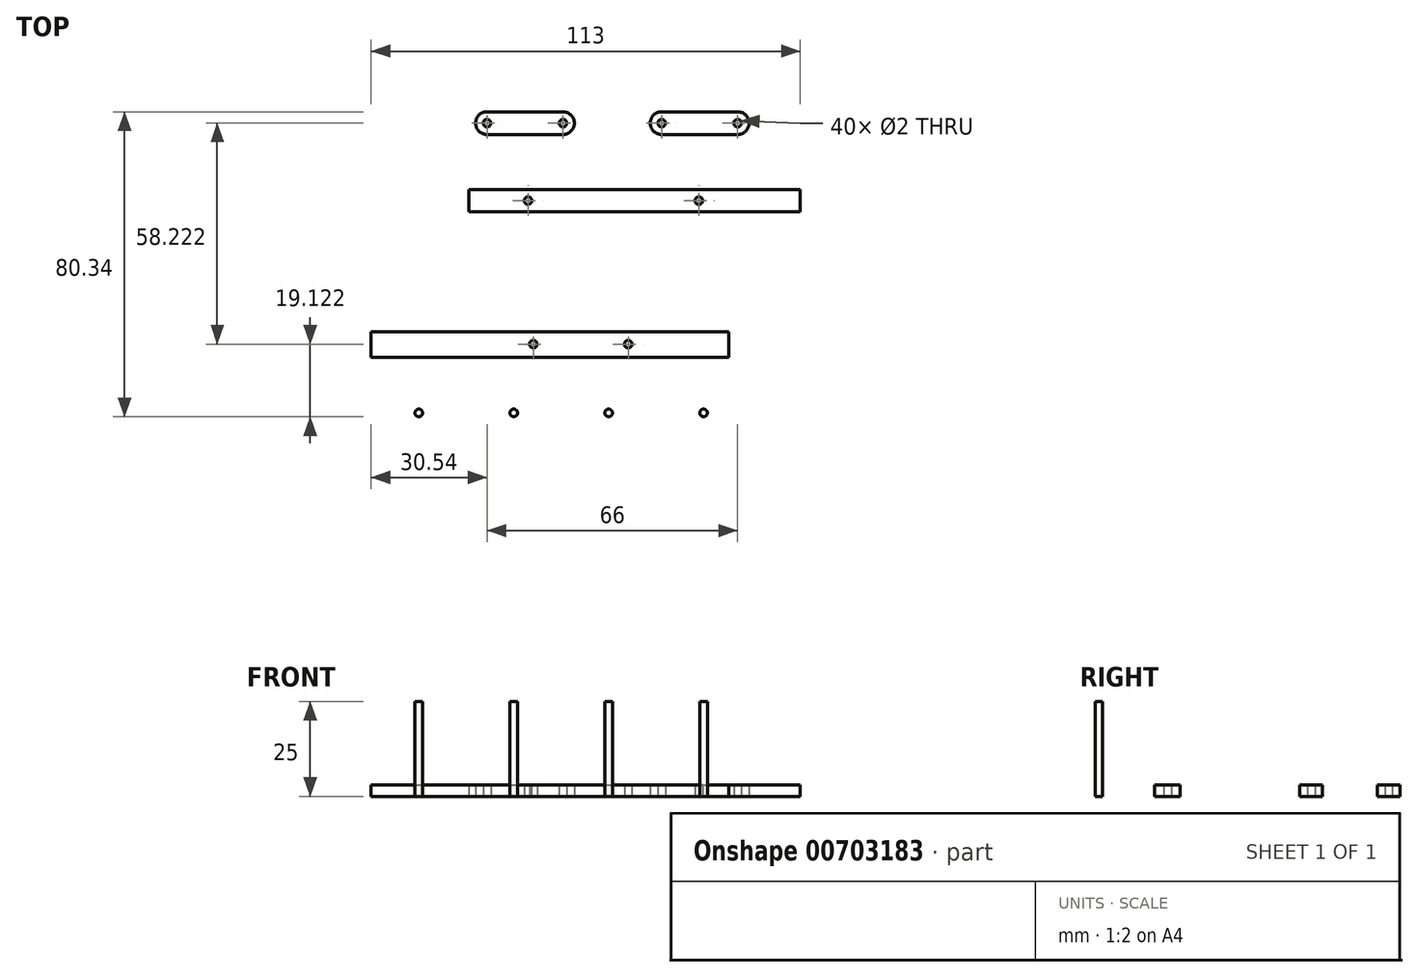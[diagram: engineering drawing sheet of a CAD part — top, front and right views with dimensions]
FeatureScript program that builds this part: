
annotation { "Feature Type Name" : "Feature", "Feature Type Description" : "" }
export const myFeature = defineFeature(function(context is Context, id is Id, definition is map)
    precondition{}
    {
        {
            var Q0;
            Q0=qCreatedBy(makeId("Top.planeOp"),FACE);
            var sketch = newSketch(context, id + "F0", { "sketchPlane" : qUnion([Q0])});
            skLineSegment(sketch, "E0.bottom", {"start": v(-41.5, 34.19) * mm, "end": v(45.78, 34.19) * mm});
            skLineSegment(sketch, "E0.top", {"start": v(-41.5, 28.31) * mm, "end": v(45.78, 28.31) * mm});
            skLineSegment(sketch, "E0.left", {"start": v(-41.5, 34.19) * mm, "end": v(-41.5, 28.31) * mm});
            skLineSegment(sketch, "E0.right", {"start": v(45.78, 34.19) * mm, "end": v(45.78, 28.31) * mm});
            skLineSegment(sketch, "E1.bottom", {"start": v(-67.22, -3.28) * mm, "end": v(26.94, -3.28) * mm});
            skLineSegment(sketch, "E1.top", {"start": v(-67.22, -9.96) * mm, "end": v(26.94, -9.96) * mm});
            skLineSegment(sketch, "E1.left", {"start": v(-67.22, -3.28) * mm, "end": v(-67.22, -9.96) * mm});
            skLineSegment(sketch, "E1.right", {"start": v(26.94, -3.28) * mm, "end": v(26.94, -9.96) * mm});
            skCircle(sketch, "E2", {"center": v(0.5, -6.52) * mm, "radius": 1 * mm});
            skCircle(sketch, "E3", {"center": v(-24.5, -6.52) * mm, "radius": 1 * mm});
            skCircle(sketch, "E4", {"center": v(-25.89, 31.28) * mm, "radius": 1 * mm});
            skCircle(sketch, "E5", {"center": v(19.11, 31.28) * mm, "radius": 1 * mm});
            skLineSegment(sketch, "E6.top", {"start": v(-36.68, 48.7) * mm, "end": v(-16.68, 48.7) * mm});
            skCircle(sketch, "E7", {"center": v(-36.68, 51.7) * mm, "radius": 1 * mm});
            skCircle(sketch, "E8", {"center": v(-16.68, 51.7) * mm, "radius": 1 * mm});
            skArc(sketch, "E9", {"start": v(-36.67, 54.7) * mm, "mid": v(-39.68, 51.7) * mm, "end": v(-36.68, 48.7) * mm});
            skArc(sketch, "E10", {"start": v(-16.68, 48.7) * mm, "mid": v(-13.68, 51.7) * mm, "end": v(-16.68, 54.7) * mm});
            skLineSegment(sketch, "E11", {"start": v(-36.67, 54.7) * mm, "end": v(-16.68, 54.7) * mm});
            skArc(sketch, "E12.1.0.0", {"start": v(9.33, 54.7) * mm, "mid": v(6.32, 51.7) * mm, "end": v(9.32, 48.7) * mm});
            skLineSegment(sketch, "E12.1.0.1", {"start": v(9.33, 54.7) * mm, "end": v(29.32, 54.7) * mm});
            skArc(sketch, "E12.1.0.2", {"start": v(29.32, 48.7) * mm, "mid": v(32.32, 51.7) * mm, "end": v(29.32, 54.7) * mm});
            skLineSegment(sketch, "E12.1.0.3", {"start": v(9.32, 48.7) * mm, "end": v(29.32, 48.7) * mm});
            skCircle(sketch, "E12.1.0.4", {"center": v(29.32, 51.7) * mm, "radius": 1 * mm});
            skCircle(sketch, "E12.1.0.5", {"center": v(9.32, 51.7) * mm, "radius": 1 * mm});
            skLineSegment(sketch, "E12.direction1", {"start": v(-36.68, 48.7) * mm, "end": v(9.32, 48.7) * mm, "construction": true});
            skSolve(sketch);
        }
        {
            var Q0;
            Q0 = qSketchRegion(id + "F0", true);
            extrude(context, id + "F1", {"entities" : qUnion([Q0]), "depth" : 3 * mm, "offsetDistance" : 25 * mm});
        }
        {
            var Q0;
            Q0=qCreatedBy(makeId("Top.planeOp"),FACE);
            var sketch = newSketch(context, id + "F2", { "sketchPlane" : qUnion([Q0])});
            skCircle(sketch, "E13", {"center": v(-54.65, -24.64) * mm, "radius": 1 * mm});
            skCircle(sketch, "E14.1.0.0", {"center": v(-29.65, -24.64) * mm, "radius": 1 * mm});
            skCircle(sketch, "E14.2.0.0", {"center": v(-4.65, -24.64) * mm, "radius": 1 * mm});
            skCircle(sketch, "E14.3.0.0", {"center": v(20.35, -24.64) * mm, "radius": 1 * mm});
            skLineSegment(sketch, "E14.direction1", {"start": v(-54.65, -24.64) * mm, "end": v(-29.65, -24.64) * mm, "construction": true});
            skSolve(sketch);
        }
        {
            var Q0;
            Q0=makeQuery(id+"F2.imprint","IMPRINT",FACE,{"disambiguationData":[TD([[makeQuery(id+"F2.imprint","IMPRINT",EDGE,{"derivedFrom":sQuery(id+"F2.wireOp",EDGE,"E13")}),1.0]])]});
            var Q1;
            Q1=makeQuery(id+"F2.imprint","IMPRINT",FACE,{"disambiguationData":[TD([[makeQuery(id+"F2.imprint","IMPRINT",EDGE,{"derivedFrom":sQuery(id+"F2.wireOp",EDGE,"E14.1.0.0")}),1.0]])]});
            var Q2;
            Q2=makeQuery(id+"F2.imprint","IMPRINT",FACE,{"disambiguationData":[TD([[makeQuery(id+"F2.imprint","IMPRINT",EDGE,{"derivedFrom":sQuery(id+"F2.wireOp",EDGE,"E14.2.0.0")}),1.0]])]});
            var Q3;
            Q3=makeQuery(id+"F2.imprint","IMPRINT",FACE,{"disambiguationData":[TD([[makeQuery(id+"F2.imprint","IMPRINT",EDGE,{"derivedFrom":sQuery(id+"F2.wireOp",EDGE,"E14.3.0.0")}),1.0]])]});
            extrude(context, id + "F3", {"entities" : qUnion([Q0, Q1, Q2, Q3]), "depth" : 25 * mm, "offsetDistance" : 25 * mm});
        }
    });
